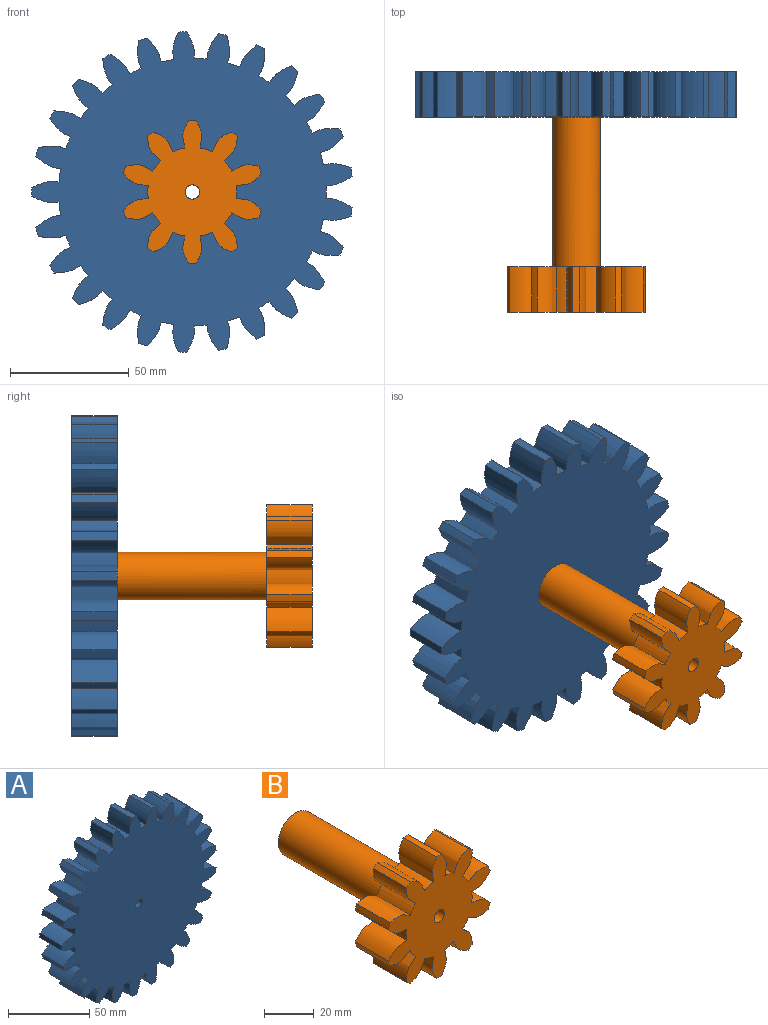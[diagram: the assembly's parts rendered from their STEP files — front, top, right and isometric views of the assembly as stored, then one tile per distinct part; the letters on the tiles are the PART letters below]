
ASSEMBLY  parts=2 mates=1
PART A: 103 faces, bbox 134.8x19x135.1 mm
  f0: cylinder r=67.5mm len=19mm, axis (0,1,0), area 68.3mm2, adj f26,f27,f79,f102
  f1: cylinder r=67.5mm len=19mm, axis (0,1,0), area 68.3mm2, adj f26,f27,f99,f100
  f2: cylinder r=67.5mm len=19mm, axis (0,1,0), area 68.3mm2, adj f26,f27,f91,f96
  f3: cylinder r=67.5mm len=19mm, axis (0,1,0), area 68.3mm2, adj f26,f27,f93,f97
  f4: cylinder r=67.5mm len=19mm, axis (0,1,0), area 68.3mm2, adj f26,f27,f85,f90
  f5: cylinder r=67.5mm len=19mm, axis (0,1,0), area 68.3mm2, adj f26,f27,f76,f87
  f6: cylinder r=67.5mm len=19mm, axis (0,1,0), area 68.3mm2, adj f26,f27,f84,f88
  f7: cylinder r=67.5mm len=19mm, axis (0,1,0), area 68.3mm2, adj f26,f27,f81,f82
  f8: cylinder r=67.5mm len=19mm, axis (0,1,0), area 68.3mm2, adj f26,f27,f73,f78
  f9: cylinder r=67.5mm len=19mm, axis (0,1,0), area 68.3mm2, adj f26,f27,f70,f75
  f10: cylinder r=67.5mm len=19mm, axis (0,1,0), area 68.3mm2, adj f26,f27,f67,f72
  f11: cylinder r=67.5mm len=19mm, axis (0,1,0), area 68.3mm2, adj f26,f27,f58,f69
  f12: cylinder r=67.5mm len=19mm, axis (0,1,0), area 68.3mm2, adj f26,f27,f28,f66
  f13: cylinder r=67.5mm len=19mm, axis (0,1,0), area 68.3mm2, adj f26,f27,f63,f64
  f14: cylinder r=67.5mm len=19mm, axis (0,1,0), area 68.3mm2, adj f26,f27,f55,f60
  f15: cylinder r=67.5mm len=19mm, axis (0,1,0), area 68.3mm2, adj f26,f27,f57,f61
  f16: cylinder r=67.5mm len=19mm, axis (0,1,0), area 68.3mm2, adj f26,f27,f54,f94
  f17: cylinder r=67.5mm len=19mm, axis (0,1,0), area 68.3mm2, adj f26,f27,f51,f52
  f18: cylinder r=67.5mm len=19mm, axis (0,1,0), area 68.3mm2, adj f26,f27,f48,f49
  f19: cylinder r=67.5mm len=19mm, axis (0,1,0), area 68.3mm2, adj f26,f27,f45,f46
  f20: cylinder r=67.5mm len=19mm, axis (0,1,0), area 68.3mm2, adj f26,f27,f37,f42
  f21: cylinder r=67.5mm len=19mm, axis (0,1,0), area 68.3mm2, adj f26,f27,f31,f39
  f22: cylinder r=67.5mm len=19mm, axis (0,1,0), area 68.3mm2, adj f26,f27,f36,f43
  f23: cylinder r=67.5mm len=19mm, axis (0,1,0), area 68.3mm2, adj f26,f27,f33,f34
  f24: cylinder r=3mm len=19mm, axis (0,1,0), area 358.1mm2, adj f26,f27
  f25: cylinder r=67.5mm len=19mm, axis (0,1,0), area 68.3mm2, adj f26,f27,f30,f40
  f26: plane 135.06x134.8mm, normal (0,-1,0), area 12025.7mm2, adj f0,f1,f2,f3,f4,f5,f6,f7
  f27: plane 135.06x134.8mm, normal (0,1,0), area 12025.7mm2, adj f0,f1,f2,f3,f4,f5,f6,f7
  f28: extruded ~19x10.98mm, area 226.1mm2, adj f12,f26,f27,f29
  f29: cylinder r=56.25mm len=19mm, axis (0,1,0), area 102.4mm2, adj f26,f27,f28,f30
  f30: extruded ~19x10.98mm, area 226.1mm2, adj f25,f26,f27,f29
  f31: extruded ~19x10.73mm, area 226.1mm2, adj f21,f26,f27,f32
  f32: cylinder r=56.25mm len=19mm, axis (0,1,0), area 102.4mm2, adj f26,f27,f31,f33
  f33: extruded ~19x10.42mm, area 226.1mm2, adj f23,f26,f27,f32
  f34: extruded ~19x9.25mm, area 226.1mm2, adj f23,f26,f27,f35
  f35: cylinder r=56.25mm len=19mm, axis (0,1,0), area 102.4mm2, adj f26,f27,f34,f36
  f36: extruded ~19x11.41mm, area 226.1mm2, adj f22,f26,f27,f35
  f37: extruded ~19x11.54mm, area 226.1mm2, adj f20,f26,f27,f38
  f38: cylinder r=56.25mm len=19mm, axis (0,1,0), area 102.4mm2, adj f26,f27,f37,f39
  f39: extruded ~19x8.78mm, area 226.1mm2, adj f21,f26,f27,f38
  f40: extruded ~19x11.63mm, area 226.1mm2, adj f25,f26,f27,f41
  f41: cylinder r=56.25mm len=19mm, axis (0,1,0), area 102.4mm2, adj f26,f27,f40,f42
  f42: extruded ~19x9.65mm, area 226.1mm2, adj f20,f26,f27,f41
  f43: extruded ~19x9.22mm, area 226.1mm2, adj f22,f26,f27,f44
  f44: cylinder r=56.25mm len=19mm, axis (0,1,0), area 102.4mm2, adj f26,f27,f43,f45
  f45: extruded ~19x11.68mm, area 226.1mm2, adj f19,f26,f27,f44
  f46: extruded ~19x10.71mm, area 226.1mm2, adj f19,f26,f27,f47
  f47: cylinder r=56.25mm len=19mm, axis (0,1,0), area 102.4mm2, adj f26,f27,f46,f48
  f48: extruded ~19x11.21mm, area 226.1mm2, adj f18,f26,f27,f47
  f49: extruded ~19x11.54mm, area 226.1mm2, adj f18,f26,f27,f50
  f50: cylinder r=56.25mm len=19mm, axis (0,1,0), area 102.4mm2, adj f26,f27,f49,f51
  f51: extruded ~19x10.04mm, area 226.1mm2, adj f17,f26,f27,f50
  f52: extruded ~19x11.63mm, area 226.1mm2, adj f17,f26,f27,f53
  f53: cylinder r=56.25mm len=19mm, axis (0,1,0), area 102.4mm2, adj f26,f27,f52,f54
  f54: extruded ~19x8.28mm, area 226.1mm2, adj f16,f26,f27,f53
  f55: extruded ~19x10.42mm, area 226.1mm2, adj f14,f26,f27,f56
  f56: cylinder r=56.25mm len=19mm, axis (0,1,0), area 102.4mm2, adj f26,f27,f55,f57
  f57: extruded ~19x10.73mm, area 226.1mm2, adj f15,f26,f27,f56
  f58: extruded ~19x11.41mm, area 226.1mm2, adj f11,f26,f27,f59
  f59: cylinder r=56.25mm len=19mm, axis (0,1,0), area 102.4mm2, adj f26,f27,f58,f60
  f60: extruded ~19x9.25mm, area 226.1mm2, adj f14,f26,f27,f59
  f61: extruded ~19x8.78mm, area 226.1mm2, adj f15,f26,f27,f62
  f62: cylinder r=56.25mm len=19mm, axis (0,1,0), area 102.4mm2, adj f26,f27,f61,f63
  f63: extruded ~19x11.54mm, area 226.1mm2, adj f13,f26,f27,f62
  f64: extruded ~19x9.65mm, area 226.1mm2, adj f13,f26,f27,f65
  f65: cylinder r=56.25mm len=19mm, axis (0,1,0), area 102.4mm2, adj f26,f27,f64,f66
  f66: extruded ~19x11.63mm, area 226.1mm2, adj f12,f26,f27,f65
  f67: extruded ~19x11.68mm, area 226.1mm2, adj f10,f26,f27,f68
  f68: cylinder r=56.25mm len=19mm, axis (0,1,0), area 102.4mm2, adj f26,f27,f67,f69
  f69: extruded ~19x9.22mm, area 226.1mm2, adj f11,f26,f27,f68
  f70: extruded ~19x11.21mm, area 226.1mm2, adj f9,f26,f27,f71
  f71: cylinder r=56.25mm len=19mm, axis (0,1,0), area 102.4mm2, adj f26,f27,f70,f72
  f72: extruded ~19x10.71mm, area 226.1mm2, adj f10,f26,f27,f71
  f73: extruded ~19x10.04mm, area 226.1mm2, adj f8,f26,f27,f74
  f74: cylinder r=56.25mm len=19mm, axis (0,1,0), area 102.4mm2, adj f26,f27,f73,f75
  f75: extruded ~19x11.54mm, area 226.1mm2, adj f9,f26,f27,f74
  f76: extruded ~19x8.28mm, area 226.1mm2, adj f5,f26,f27,f77
  f77: cylinder r=56.25mm len=19mm, axis (0,1,0), area 102.4mm2, adj f26,f27,f76,f78
  f78: extruded ~19x11.63mm, area 226.1mm2, adj f8,f26,f27,f77
  f79: extruded ~19x11.4mm, area 226.1mm2, adj f0,f26,f27,f80
  f80: cylinder r=56.25mm len=19mm, axis (0,1,0), area 102.4mm2, adj f26,f27,f79,f81
  f81: extruded ~19x10.4mm, area 226.1mm2, adj f7,f26,f27,f80
  f82: extruded ~19x11.68mm, area 226.1mm2, adj f7,f26,f27,f83
  f83: cylinder r=56.25mm len=19mm, axis (0,1,0), area 102.4mm2, adj f26,f27,f82,f84
  f84: extruded ~19x8.75mm, area 226.1mm2, adj f6,f26,f27,f83
  f85: extruded ~19x10.07mm, area 226.1mm2, adj f4,f26,f27,f86
  f86: cylinder r=56.25mm len=19mm, axis (0,1,0), area 102.4mm2, adj f26,f27,f85,f87
  f87: extruded ~19x11mm, area 226.1mm2, adj f5,f26,f27,f86
  f88: extruded ~19x11.23mm, area 226.1mm2, adj f6,f26,f27,f89
  f89: cylinder r=56.25mm len=19mm, axis (0,1,0), area 102.4mm2, adj f26,f27,f88,f90
  f90: extruded ~19x9.68mm, area 226.1mm2, adj f4,f26,f27,f89
  f91: extruded ~19x9.68mm, area 226.1mm2, adj f2,f26,f27,f92
  f92: cylinder r=56.25mm len=19mm, axis (0,1,0), area 102.4mm2, adj f26,f27,f91,f93
  f93: extruded ~19x11.23mm, area 226.1mm2, adj f3,f26,f27,f92
  f94: extruded ~19x11mm, area 226.1mm2, adj f16,f26,f27,f95
  f95: cylinder r=56.25mm len=19mm, axis (0,1,0), area 102.4mm2, adj f26,f27,f94,f96
  f96: extruded ~19x10.07mm, area 226.1mm2, adj f2,f26,f27,f95
  f97: extruded ~19x8.75mm, area 226.1mm2, adj f3,f26,f27,f98
  f98: cylinder r=56.25mm len=19mm, axis (0,1,0), area 102.4mm2, adj f26,f27,f97,f99
  f99: extruded ~19x11.68mm, area 226.1mm2, adj f1,f26,f27,f98
  f100: extruded ~19x10.4mm, area 226.1mm2, adj f1,f26,f27,f101
  f101: cylinder r=56.25mm len=19mm, axis (0,1,0), area 102.4mm2, adj f26,f27,f100,f102
  f102: extruded ~19x11.4mm, area 226.1mm2, adj f0,f26,f27,f101
PART B: 45 faces, bbox 58x82x60.1 mm
  f0: cylinder r=30mm len=19mm, axis (0,-1,0), area 55.8mm2, adj f10,f11,f37,f42
  f1: cylinder r=30mm len=19mm, axis (0,-1,0), area 55.8mm2, adj f10,f11,f13,f39
  f2: cylinder r=30mm len=19mm, axis (0,-1,0), area 55.8mm2, adj f10,f11,f31,f36
  f3: cylinder r=30mm len=19mm, axis (0,-1,0), area 55.8mm2, adj f10,f11,f33,f40
  f4: cylinder r=30mm len=19mm, axis (0,-1,0), area 55.8mm2, adj f10,f11,f25,f30
  f5: cylinder r=30mm len=19mm, axis (0,-1,0), area 55.8mm2, adj f10,f11,f22,f27
  f6: cylinder r=30mm len=19mm, axis (0,-1,0), area 55.8mm2, adj f10,f11,f19,f24
  f7: cylinder r=30mm len=19mm, axis (0,-1,0), area 55.8mm2, adj f10,f11,f21,f34
  f8: cylinder r=30mm len=19mm, axis (0,-1,0), area 55.8mm2, adj f10,f11,f18,f28
  f9: cylinder r=30mm len=19mm, axis (0,-1,0), area 55.8mm2, adj f10,f11,f15,f16
  f10: plane 60.1x58.03mm, normal (0,1,0), area 1548.4mm2, adj f0,f1,f2,f3,f4,f5,f6,f7
  f11: plane 60.1x58.03mm, normal (0,-1,0), area 1834.3mm2, adj f0,f1,f2,f3,f4,f5,f6,f7
  f12: cylinder r=3mm len=82mm, axis (0,-1,0), area 1545.7mm2, adj f11,f44
  f13: extruded ~19x10.39mm, area 232.8mm2, adj f1,f10,f11,f14
  f14: cylinder r=18.75mm len=19mm, axis (0,-1,0), area 101.3mm2, adj f10,f11,f13,f15
  f15: extruded ~19x10.39mm, area 232.8mm2, adj f9,f10,f11,f14
  f16: extruded ~19x11.47mm, area 232.8mm2, adj f9,f10,f11,f17
  f17: cylinder r=18.75mm len=19mm, axis (0,-1,0), area 101.3mm2, adj f10,f11,f16,f18
  f18: extruded ~19x10.32mm, area 232.8mm2, adj f8,f10,f11,f17
  f19: extruded ~19x10.39mm, area 232.8mm2, adj f6,f10,f11,f20
  f20: cylinder r=18.75mm len=19mm, axis (0,-1,0), area 101.3mm2, adj f10,f11,f19,f21
  f21: extruded ~19x10.39mm, area 232.8mm2, adj f7,f10,f11,f20
  f22: extruded ~19x10.32mm, area 232.8mm2, adj f5,f10,f11,f23
  f23: cylinder r=18.75mm len=19mm, axis (0,-1,0), area 101.3mm2, adj f10,f11,f22,f24
  f24: extruded ~19x11.47mm, area 232.8mm2, adj f6,f10,f11,f23
  f25: extruded ~19x11.49mm, area 232.8mm2, adj f4,f10,f11,f26
  f26: cylinder r=18.75mm len=19mm, axis (0,-1,0), area 101.3mm2, adj f10,f11,f25,f27
  f27: extruded ~19x8.27mm, area 232.8mm2, adj f5,f10,f11,f26
  f28: extruded ~19x8.27mm, area 232.8mm2, adj f8,f10,f11,f29
  f29: cylinder r=18.75mm len=19mm, axis (0,-1,0), area 101.3mm2, adj f10,f11,f28,f30
  f30: extruded ~19x11.49mm, area 232.8mm2, adj f4,f10,f11,f29
  f31: extruded ~19x8.27mm, area 232.8mm2, adj f2,f10,f11,f32
  f32: cylinder r=18.75mm len=19mm, axis (0,-1,0), area 101.3mm2, adj f10,f11,f31,f33
  f33: extruded ~19x11.49mm, area 232.8mm2, adj f3,f10,f11,f32
  f34: extruded ~19x11.47mm, area 232.8mm2, adj f7,f10,f11,f35
  f35: cylinder r=18.75mm len=19mm, axis (0,-1,0), area 101.3mm2, adj f10,f11,f34,f36
  f36: extruded ~19x10.32mm, area 232.8mm2, adj f2,f10,f11,f35
  f37: extruded ~19x10.32mm, area 232.8mm2, adj f0,f10,f11,f38
  f38: cylinder r=18.75mm len=19mm, axis (0,-1,0), area 101.3mm2, adj f10,f11,f37,f39
  f39: extruded ~19x11.47mm, area 232.8mm2, adj f1,f10,f11,f38
  f40: extruded ~19x11.49mm, area 232.8mm2, adj f3,f10,f11,f41
  f41: cylinder r=18.75mm len=19mm, axis (0,-1,0), area 101.3mm2, adj f10,f11,f40,f42
  f42: extruded ~19x8.27mm, area 232.8mm2, adj f0,f10,f11,f41
  f43: cylinder r=10mm len=63mm, axis (0,-1,0), area 3958.4mm2, adj f10,f44
  f44: plane 20x20mm, normal (0,1,0), area 285.9mm2, adj f12,f43
PLACE A t=(-3.43,80.11,19.03)mm
PLACE B t=(-3.43,-20.89,19.03)mm
MATE fastened A.f0 <-> B.f43  axis (0,-1,0) through (-3.43,61.11,19.03)mm
